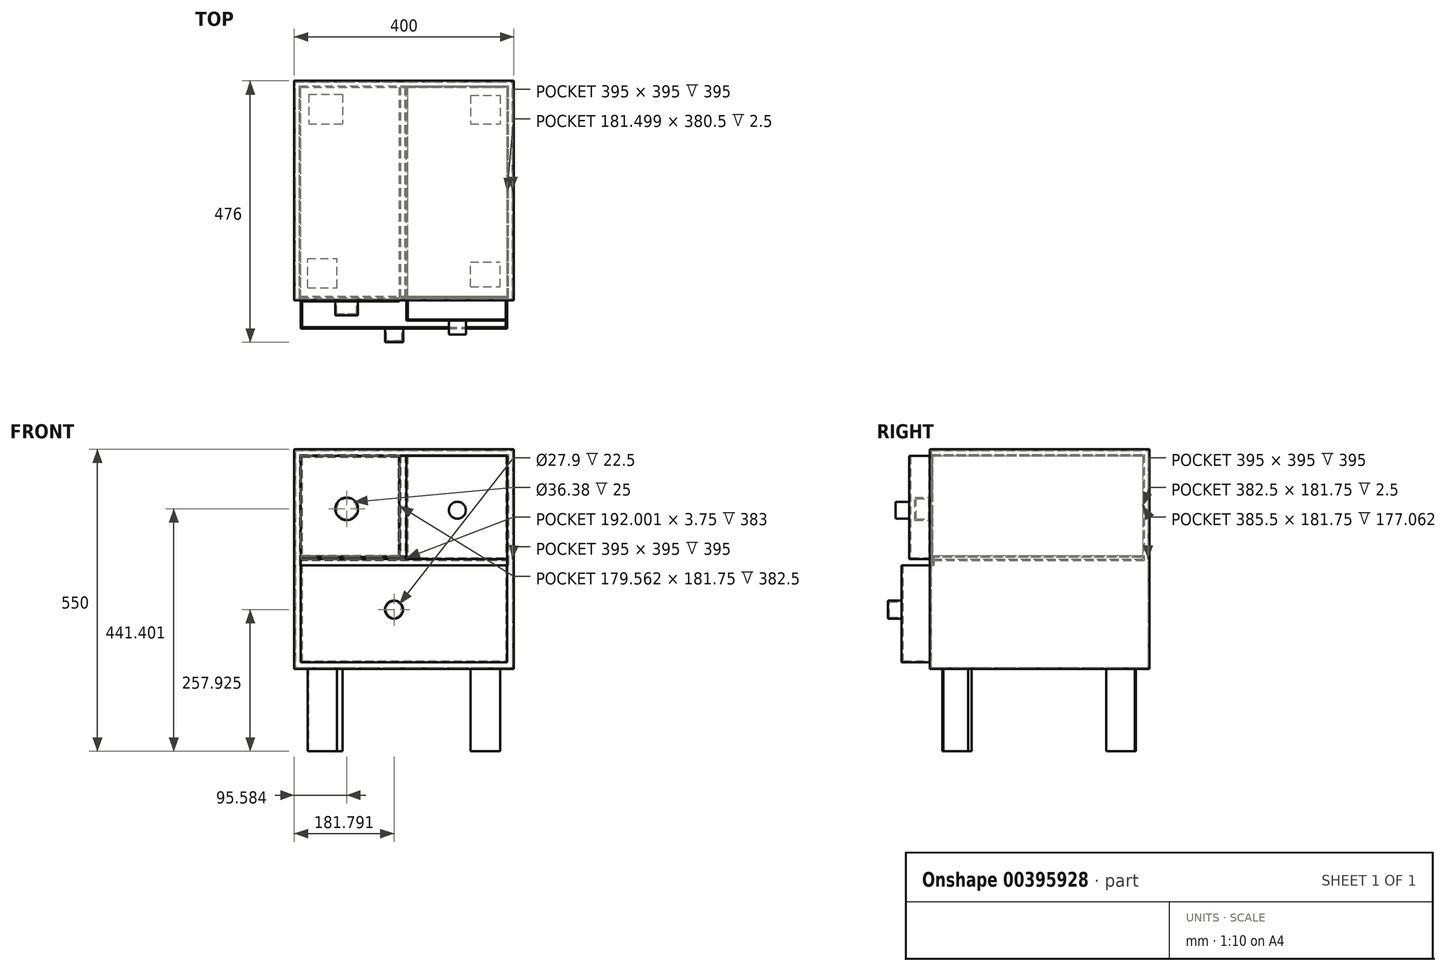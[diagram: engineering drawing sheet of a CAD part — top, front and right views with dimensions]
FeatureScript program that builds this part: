
annotation { "Feature Type Name" : "Feature", "Feature Type Description" : "" }
export const myFeature = defineFeature(function(context is Context, id is Id, definition is map)
    precondition{}
    {
        {
            var Q0;
            Q0=qCreatedBy(makeId("Top.planeOp"),FACE);
            var sketch = newSketch(context, id + "F0", { "sketchPlane" : qUnion([Q0])});
            skLineSegment(sketch, "E0.bottom", {"start": v(-204, -111.1) * mm, "end": v(196, -111.1) * mm});
            skLineSegment(sketch, "E0.top", {"start": v(-204, 288.9) * mm, "end": v(196, 288.9) * mm});
            skLineSegment(sketch, "E0.left", {"start": v(-204, -111.1) * mm, "end": v(-204, 288.9) * mm});
            skLineSegment(sketch, "E0.right", {"start": v(196, -111.1) * mm, "end": v(196, 288.9) * mm});
            skSolve(sketch);
        }
        {
            var Q0;
            Q0 = qSketchRegion(id + "F0", true);
            extrude(context, id + "F1", {"entities" : qUnion([Q0]), "depth" : 400 * mm});
        }
        {
            var Q0;
            Q0=makeQuery(id+"F1.opExtrude","SWEPT_FACE",FACE,{"disambiguationData":[OSD([sQuery(id+"F0.wireOp",EDGE,"E0.bottom")])]});
            shell(context, id + "F2", {"entities" : qUnion([Q0]), "thickness" : 12 * mm});
        }
        {
            var Q0;
            Q0=makeQuery(id+"F2.opShell","OFFSET_FACE",FACE,{"disambiguationData":[OSD([sQuery(id+"F0.wireOp",EDGE,"E0.top")])]});
            var sketch = newSketch(context, id + "F3", { "sketchPlane" : qUnion([Q0])});
            skLineSegment(sketch, "E1.bottom", {"start": v(-12.44, 388) * mm, "end": v(0, 388) * mm});
            skLineSegment(sketch, "E1.top", {"start": v(-12.44, 203.75) * mm, "end": v(0, 203.75) * mm});
            skLineSegment(sketch, "E1.left", {"start": v(-12.44, 388) * mm, "end": v(-12.44, 203.75) * mm});
            skLineSegment(sketch, "E1.right", {"start": v(0, 388) * mm, "end": v(0, 203.75) * mm});
            skSolve(sketch);
        }
        {
            var Q0;
            Q0 = qSketchRegion(id + "F3", true);
            extrude(context, id + "F4", {"entities" : qUnion([Q0]), "operationType" : NewBodyOperationType.ADD, "depth" : 385 * mm});
        }
        {
            var Q0;
            Q0=makeQuery(id+"F2.opShell","OFFSET_FACE",FACE,{"disambiguationData":[OSD([sQuery(id+"F0.wireOp",EDGE,"E0.top")])]});
            var sketch = newSketch(context, id + "F5", { "sketchPlane" : qUnion([Q0])});
            skLineSegment(sketch, "E2.bottom", {"start": v(-192, 200) * mm, "end": v(184, 200) * mm});
            skLineSegment(sketch, "E2.top", {"start": v(-192, 188.75) * mm, "end": v(184, 188.75) * mm});
            skLineSegment(sketch, "E2.left", {"start": v(-192, 200) * mm, "end": v(-192, 188.75) * mm});
            skLineSegment(sketch, "E2.right", {"start": v(184, 200) * mm, "end": v(184, 188.75) * mm});
            skSolve(sketch);
        }
        {
            var Q0;
            Q0 = qSketchRegion(id + "F5", true);
            extrude(context, id + "F6", {"entities" : qUnion([Q0]), "operationType" : NewBodyOperationType.ADD, "depth" : 383 * mm});
        }
        {
            var Q0;
            {var subQ2=sQuery(id+"F0.wireOp",EDGE,"E0.top");Q0=makeQuery(id+"F6.boolean.opBoolean","SPLIT",FACE,{"disambiguationData":[TD([makeQuery(id+"F6.opExtrude","SWEPT_FACE",FACE,{"disambiguationData":[OSD([sQuery(id+"F5.wireOp",EDGE,"E2.top")])]})])],"derivedFrom":makeQuery(id+"F2.opShell","OFFSET_FACE",FACE,{"disambiguationData":[OSD([subQ2])]})});}
            var sketch = newSketch(context, id + "F7", { "sketchPlane" : qUnion([Q0])});
            skLineSegment(sketch, "E3.bottom", {"start": v(-192, 188.75) * mm, "end": v(184, 188.75) * mm});
            skLineSegment(sketch, "E3.top", {"start": v(-192, 12) * mm, "end": v(184, 12) * mm});
            skLineSegment(sketch, "E3.left", {"start": v(-192, 188.75) * mm, "end": v(-192, 12) * mm});
            skLineSegment(sketch, "E3.right", {"start": v(184, 188.75) * mm, "end": v(184, 12) * mm});
            skSolve(sketch);
        }
        {
            var Q0;
            Q0 = qSketchRegion(id + "F7", true);
            extrude(context, id + "F8", {"entities" : qUnion([Q0]), "operationType" : NewBodyOperationType.ADD, "depth" : 439 * mm});
        }
        {
            var Q0;
            Q0=makeQuery(id+"F8.opExtrude","SWEPT_FACE",FACE,{"disambiguationData":[OSD([sQuery(id+"F7.wireOp",EDGE,"E3.bottom")])]});
            shell(context, id + "F9", {"entities" : qUnion([Q0]), "thickness" : 2.5 * mm});
        }
        {
            var Q0;
            Q0=makeQuery(id+"F8.opExtrude","CAP_FACE",FACE,{"disambiguationData":[OSD([sQuery(id+"F7.wireOp",EDGE,"E3.bottom"),sQuery(id+"F7.wireOp",EDGE,"E3.top"),sQuery(id+"F7.wireOp",EDGE,"E3.left"),sQuery(id+"F7.wireOp",EDGE,"E3.right")])],"isStart":false});
            var sketch = newSketch(context, id + "F10", { "sketchPlane" : qUnion([Q0])});
            skCircle(sketch, "E4", {"center": v(-22.2, 107.93) * mm, "radius": 16.45 * mm});
            skSolve(sketch);
        }
        {
            var Q0;
            Q0 = qSketchRegion(id + "F10", true);
            extrude(context, id + "F11", {"entities" : qUnion([Q0]), "operationType" : NewBodyOperationType.ADD, "depth" : 25 * mm});
        }
        {
            var Q0;
            {var subQ2=sQuery(id+"F0.wireOp",EDGE,"E0.top");Q0=makeQuery(id+"F6.boolean.opBoolean","SPLIT",FACE,{"disambiguationData":[TD([makeQuery(id+"F4.opExtrude","SWEPT_FACE",FACE,{"disambiguationData":[OSD([sQuery(id+"F3.wireOp",EDGE,"E1.top")])]})])],"derivedFrom":makeQuery(id+"F2.opShell","OFFSET_FACE",FACE,{"disambiguationData":[OSD([subQ2])]})});}
            var sketch = newSketch(context, id + "F12", { "sketchPlane" : qUnion([Q0])});
            skLineSegment(sketch, "E5.bottom", {"start": v(-192, 388) * mm, "end": v(-12.44, 388) * mm});
            skLineSegment(sketch, "E5.top", {"start": v(-192, 203.75) * mm, "end": v(-12.44, 203.75) * mm});
            skLineSegment(sketch, "E5.left", {"start": v(-192, 388) * mm, "end": v(-192, 203.75) * mm});
            skLineSegment(sketch, "E5.right", {"start": v(-12.44, 388) * mm, "end": v(-12.44, 203.75) * mm});
            skSolve(sketch);
        }
        {
            var Q0;
            Q0 = qSketchRegion(id + "F12", true);
            extrude(context, id + "F13", {"entities" : qUnion([Q0]), "operationType" : NewBodyOperationType.ADD, "depth" : 390 * mm});
        }
        {
            var Q0;
            Q0=makeQuery(id+"F13.opExtrude","CAP_FACE",FACE,{"disambiguationData":[OSD([sQuery(id+"F12.wireOp",EDGE,"E5.bottom"),sQuery(id+"F12.wireOp",EDGE,"E5.top"),sQuery(id+"F12.wireOp",EDGE,"E5.left"),sQuery(id+"F12.wireOp",EDGE,"E5.right")])],"isStart":false});
            var sketch = newSketch(context, id + "F14", { "sketchPlane" : qUnion([Q0])});
            skCircle(sketch, "E6", {"center": v(-108.42, 291.4) * mm, "radius": 20.69 * mm});
            skSolve(sketch);
        }
        {
            var Q0;
            Q0 = qSketchRegion(id + "F14", true);
            extrude(context, id + "F15", {"entities" : qUnion([Q0]), "operationType" : NewBodyOperationType.ADD, "depth" : 25 * mm});
        }
        {
            var Q0;
            {var subQ2=sQuery(id+"F0.wireOp",EDGE,"E0.top");Q0=makeQuery(id+"F6.boolean.opBoolean","SPLIT",FACE,{"disambiguationData":[TD([makeQuery(id+"F4.opExtrude","SWEPT_FACE",FACE,{"disambiguationData":[OSD([sQuery(id+"F3.wireOp",EDGE,"E1.top")])]})])],"derivedFrom":makeQuery(id+"F2.opShell","OFFSET_FACE",FACE,{"disambiguationData":[OSD([subQ2])]})});}
            var sketch = newSketch(context, id + "F16", { "sketchPlane" : qUnion([Q0])});
            skLineSegment(sketch, "E7.bottom", {"start": v(0, 388) * mm, "end": v(184, 388) * mm});
            skLineSegment(sketch, "E7.top", {"start": v(0, 200) * mm, "end": v(184, 200) * mm});
            skLineSegment(sketch, "E7.left", {"start": v(0, 388) * mm, "end": v(0, 200) * mm});
            skLineSegment(sketch, "E7.right", {"start": v(184, 388) * mm, "end": v(184, 200) * mm});
            skSolve(sketch);
        }
        {
            var Q0;
            Q0 = qSketchRegion(id + "F16", true);
            extrude(context, id + "F17", {"entities" : qUnion([Q0]), "operationType" : NewBodyOperationType.ADD, "depth" : 425 * mm});
        }
        {
            var Q0;
            Q0=makeQuery(id+"F17.opExtrude","SWEPT_FACE",FACE,{"disambiguationData":[OSD([sQuery(id+"F16.wireOp",EDGE,"E7.bottom")])]});
            shell(context, id + "F18", {"entities" : qUnion([Q0]), "thickness" : 2.5 * mm});
        }
        {
            var Q0;
            Q0=makeQuery(id+"F17.opExtrude","CAP_FACE",FACE,{"disambiguationData":[OSD([sQuery(id+"F16.wireOp",EDGE,"E7.bottom"),sQuery(id+"F16.wireOp",EDGE,"E7.top"),sQuery(id+"F16.wireOp",EDGE,"E7.left"),sQuery(id+"F16.wireOp",EDGE,"E7.right")])],"isStart":false});
            var sketch = newSketch(context, id + "F19", { "sketchPlane" : qUnion([Q0])});
            skCircle(sketch, "E8", {"center": v(93.04, 288.9) * mm, "radius": 15.51 * mm});
            skSolve(sketch);
        }
        {
            var Q0;
            Q0 = qSketchRegion(id + "F19", true);
            extrude(context, id + "F20", {"entities" : qUnion([Q0]), "operationType" : NewBodyOperationType.ADD, "depth" : 25 * mm});
        }
        {
            var Q0;
            Q0=makeQuery(id+"F1.opExtrude","CAP_FACE",FACE,{"disambiguationData":[OSD([sQuery(id+"F0.wireOp",EDGE,"E0.bottom"),sQuery(id+"F0.wireOp",EDGE,"E0.top"),sQuery(id+"F0.wireOp",EDGE,"E0.left"),sQuery(id+"F0.wireOp",EDGE,"E0.right")])],"isStart":true});
            var sketch = newSketch(context, id + "F21", { "sketchPlane" : qUnion([Q0])});
            skLineSegment(sketch, "E9.bottom", {"start": v(117.2, 86.26) * mm, "end": v(170.74, 86.26) * mm});
            skLineSegment(sketch, "E9.top", {"start": v(117.2, 41.16) * mm, "end": v(170.74, 41.16) * mm});
            skLineSegment(sketch, "E9.left", {"start": v(117.2, 86.26) * mm, "end": v(117.2, 41.16) * mm});
            skLineSegment(sketch, "E9.right", {"start": v(170.74, 86.26) * mm, "end": v(170.74, 41.16) * mm});
            skLineSegment(sketch, "E10.bottom", {"start": v(117.2, -263.23) * mm, "end": v(170.74, -263.23) * mm});
            skLineSegment(sketch, "E10.top", {"start": v(117.2, -210.61) * mm, "end": v(170.74, -210.61) * mm});
            skLineSegment(sketch, "E10.left", {"start": v(117.2, -263.23) * mm, "end": v(117.2, -210.61) * mm});
            skLineSegment(sketch, "E10.right", {"start": v(170.74, -263.23) * mm, "end": v(170.74, -210.61) * mm});
            skLineSegment(sketch, "E11.bottom", {"start": v(-120.5, -263.23) * mm, "end": v(-174.05, -263.23) * mm});
            skLineSegment(sketch, "E11.top", {"start": v(-120.5, -204.98) * mm, "end": v(-174.05, -204.98) * mm});
            skLineSegment(sketch, "E11.left", {"start": v(-120.5, -263.23) * mm, "end": v(-120.5, -204.98) * mm});
            skLineSegment(sketch, "E11.right", {"start": v(-174.05, -263.23) * mm, "end": v(-174.05, -204.98) * mm});
            skLineSegment(sketch, "E12.top", {"start": v(-180.62, -263.23) * mm, "end": v(-120.5, -263.23) * mm});
            skSolve(sketch);
        }
        {
            var Q0;
            Q0=makeQuery(id+"F21.imprint","IMPRINT",FACE,{"disambiguationData":[TD([[makeQuery(id+"F21.imprint","IMPRINT",EDGE,{"derivedFrom":sQuery(id+"F21.wireOp",EDGE,"E9.bottom")}),-1.0]])]});
            extrude(context, id + "F22", {"entities" : qUnion([Q0]), "operationType" : NewBodyOperationType.ADD, "depth" : 150 * mm});
        }
        {
            var Q0;
            Q0=makeQuery(id+"F1.opExtrude","CAP_FACE",FACE,{"disambiguationData":[OSD([sQuery(id+"F0.wireOp",EDGE,"E0.bottom"),sQuery(id+"F0.wireOp",EDGE,"E0.top"),sQuery(id+"F0.wireOp",EDGE,"E0.left"),sQuery(id+"F0.wireOp",EDGE,"E0.right")])],"isStart":true});
            var sketch = newSketch(context, id + "F23", { "sketchPlane" : qUnion([Q0])});
            skLineSegment(sketch, "E13.bottom", {"start": v(117.2, -262.3) * mm, "end": v(170.74, -262.3) * mm});
            skLineSegment(sketch, "E13.top", {"start": v(117.2, -210.61) * mm, "end": v(170.74, -210.61) * mm});
            skLineSegment(sketch, "E13.left", {"start": v(117.2, -262.3) * mm, "end": v(117.2, -210.61) * mm});
            skLineSegment(sketch, "E13.right", {"start": v(170.74, -262.3) * mm, "end": v(170.74, -210.61) * mm});
            skSolve(sketch);
        }
        {
            var Q0;
            Q0 = qSketchRegion(id + "F23", true);
            extrude(context, id + "F24", {"entities" : qUnion([Q0]), "operationType" : NewBodyOperationType.ADD, "depth" : 150 * mm});
        }
        {
            var Q0;
            Q0=makeQuery(id+"F1.opExtrude","CAP_FACE",FACE,{"disambiguationData":[OSD([sQuery(id+"F0.wireOp",EDGE,"E0.bottom"),sQuery(id+"F0.wireOp",EDGE,"E0.top"),sQuery(id+"F0.wireOp",EDGE,"E0.left"),sQuery(id+"F0.wireOp",EDGE,"E0.right")])],"isStart":true});
            var sketch = newSketch(context, id + "F25", { "sketchPlane" : qUnion([Q0])});
            skLineSegment(sketch, "E14.bottom", {"start": v(-177.87, -264.28) * mm, "end": v(-115.81, -264.28) * mm});
            skLineSegment(sketch, "E14.top", {"start": v(-177.87, -210.61) * mm, "end": v(-115.81, -210.61) * mm});
            skLineSegment(sketch, "E14.left", {"start": v(-177.87, -264.28) * mm, "end": v(-177.87, -210.61) * mm});
            skLineSegment(sketch, "E14.right", {"start": v(-115.81, -264.28) * mm, "end": v(-115.81, -210.61) * mm});
            skSolve(sketch);
        }
        {
            var Q0;
            Q0 = qSketchRegion(id + "F25", true);
            extrude(context, id + "F26", {"entities" : qUnion([Q0]), "operationType" : NewBodyOperationType.ADD, "depth" : 150 * mm});
        }
        {
            var Q0;
            Q0=makeQuery(id+"F25.imprint","IMPRINT",FACE,{"disambiguationData":[TD([[makeQuery(id+"F25.imprint","IMPRINT",EDGE,{"derivedFrom":sQuery(id+"F25.wireOp",EDGE,"E14.bottom")}),-1.0]])]});
            var sketch = newSketch(context, id + "F27", { "sketchPlane" : qUnion([Q0])});
            skLineSegment(sketch, "E15.bottom", {"start": v(-179.68, 88.14) * mm, "end": v(-126.13, 88.14) * mm});
            skLineSegment(sketch, "E15.top", {"start": v(-179.68, 34.59) * mm, "end": v(-126.13, 34.59) * mm});
            skLineSegment(sketch, "E15.left", {"start": v(-179.68, 88.14) * mm, "end": v(-179.68, 34.59) * mm});
            skLineSegment(sketch, "E15.right", {"start": v(-126.13, 88.14) * mm, "end": v(-126.13, 34.59) * mm});
            skSolve(sketch);
        }
        {
            var Q0;
            Q0 = qSketchRegion(id + "F27", true);
            extrude(context, id + "F28", {"entities" : qUnion([Q0]), "operationType" : NewBodyOperationType.ADD, "depth" : 150 * mm});
        }
    });
